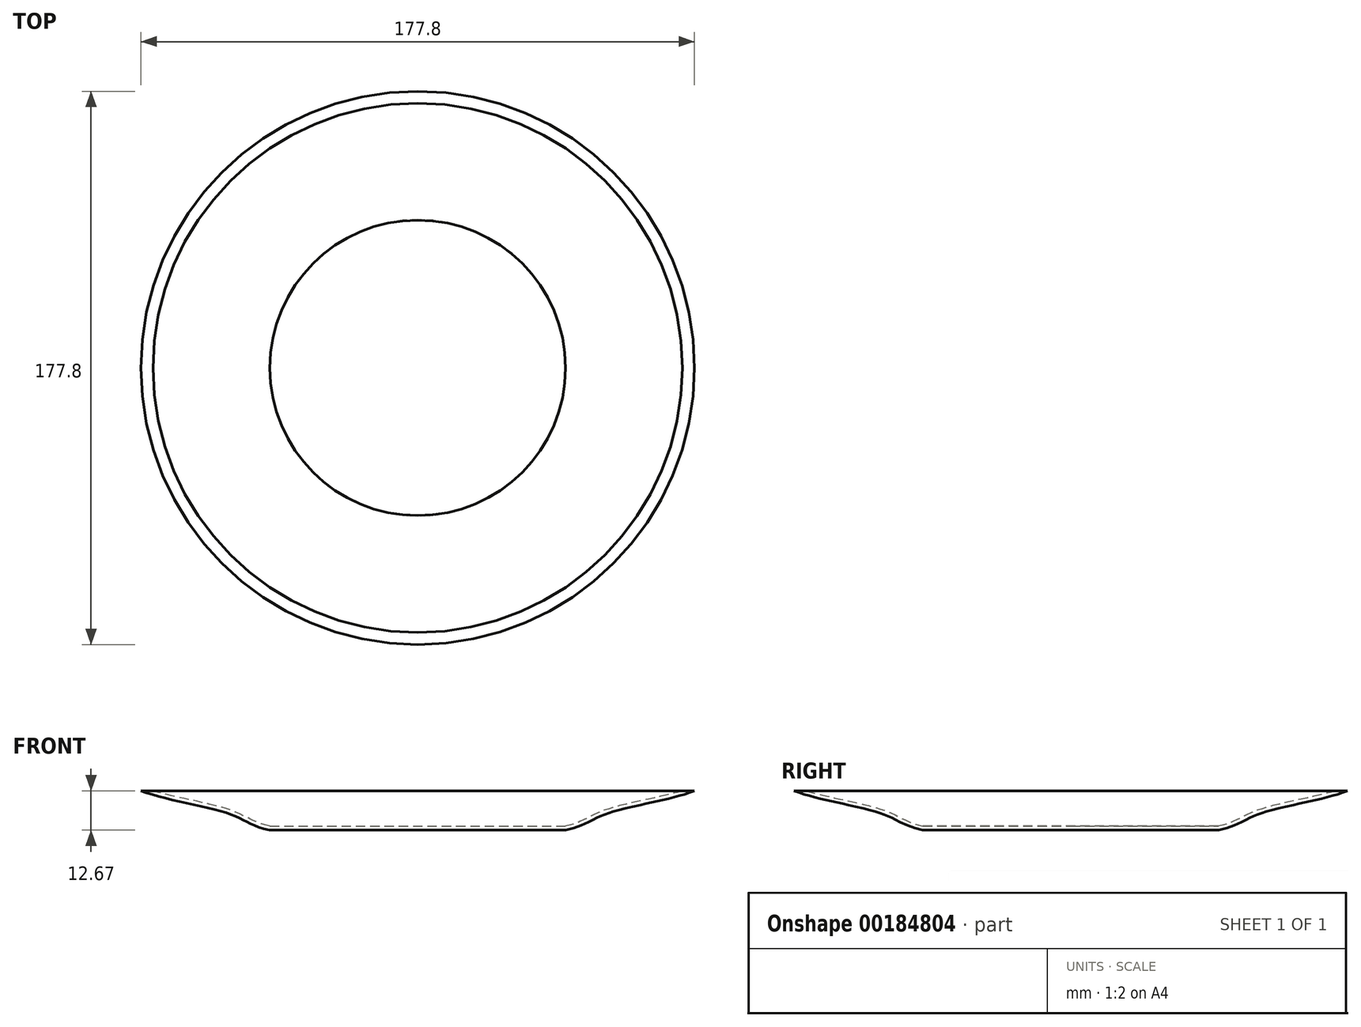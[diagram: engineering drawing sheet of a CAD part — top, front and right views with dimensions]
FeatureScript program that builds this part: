
annotation { "Feature Type Name" : "Feature", "Feature Type Description" : "" }
export const myFeature = defineFeature(function(context is Context, id is Id, definition is map)
    precondition{}
    {
        {
            var Q0;
            Q0=qCreatedBy(makeId("Front.planeOp"),FACE);
            var sketch = newSketch(context, id + "F0", { "sketchPlane" : qUnion([Q0])});
            skLineSegment(sketch, "E0", {"start": v(0, 0) * mm, "end": v(0, 12.67) * mm});
            skLineSegment(sketch, "E1", {"start": v(0, 12.67) * mm, "end": v(88.9, 12.67) * mm});
            skLineSegment(sketch, "E2", {"start": v(0, 0) * mm, "end": v(47.63, 0) * mm});
            skFitSpline(sketch, "E3", {"points": [v(47.63, 0) * mm, v(60.52, 5.24) * mm, v(88.9, 12.67) * mm], "startDerivative": vector(45.43, 10.34) * mm, "endDerivative": vector(36.97, 15.07) * mm});
            skSolve(sketch);
        }
        {
            var Q0;
            Q0=makeQuery(id+"F0.imprint","IMPRINT",FACE,{"disambiguationData":[TD([[makeQuery(id+"F0.imprint","IMPRINT",EDGE,{"derivedFrom":sQuery(id+"F0.wireOp",EDGE,"E0")}),-1.0]])]});
            var Q1;
            Q1=sQuery(id+"F0.wireOp",EDGE,"E0");
            revolve(context, id + "F1", {"surfaceOperationType" : NewSurfaceOperationType.NEW, "entities" : qUnion([Q0]), "axis" : qUnion([Q1]), "revolveType" : RevolveType.FULL});
        }
        {
            var Q0;
            Q0=makeQuery(id+"F1.opRevolve","SWEPT_FACE",FACE,{"disambiguationData":[OSD([sQuery(id+"F0.wireOp",EDGE,"E1")])]});
            shell(context, id + "F2", {"entities" : qUnion([Q0]), "thickness" : 1.27 * mm});
        }
    });
